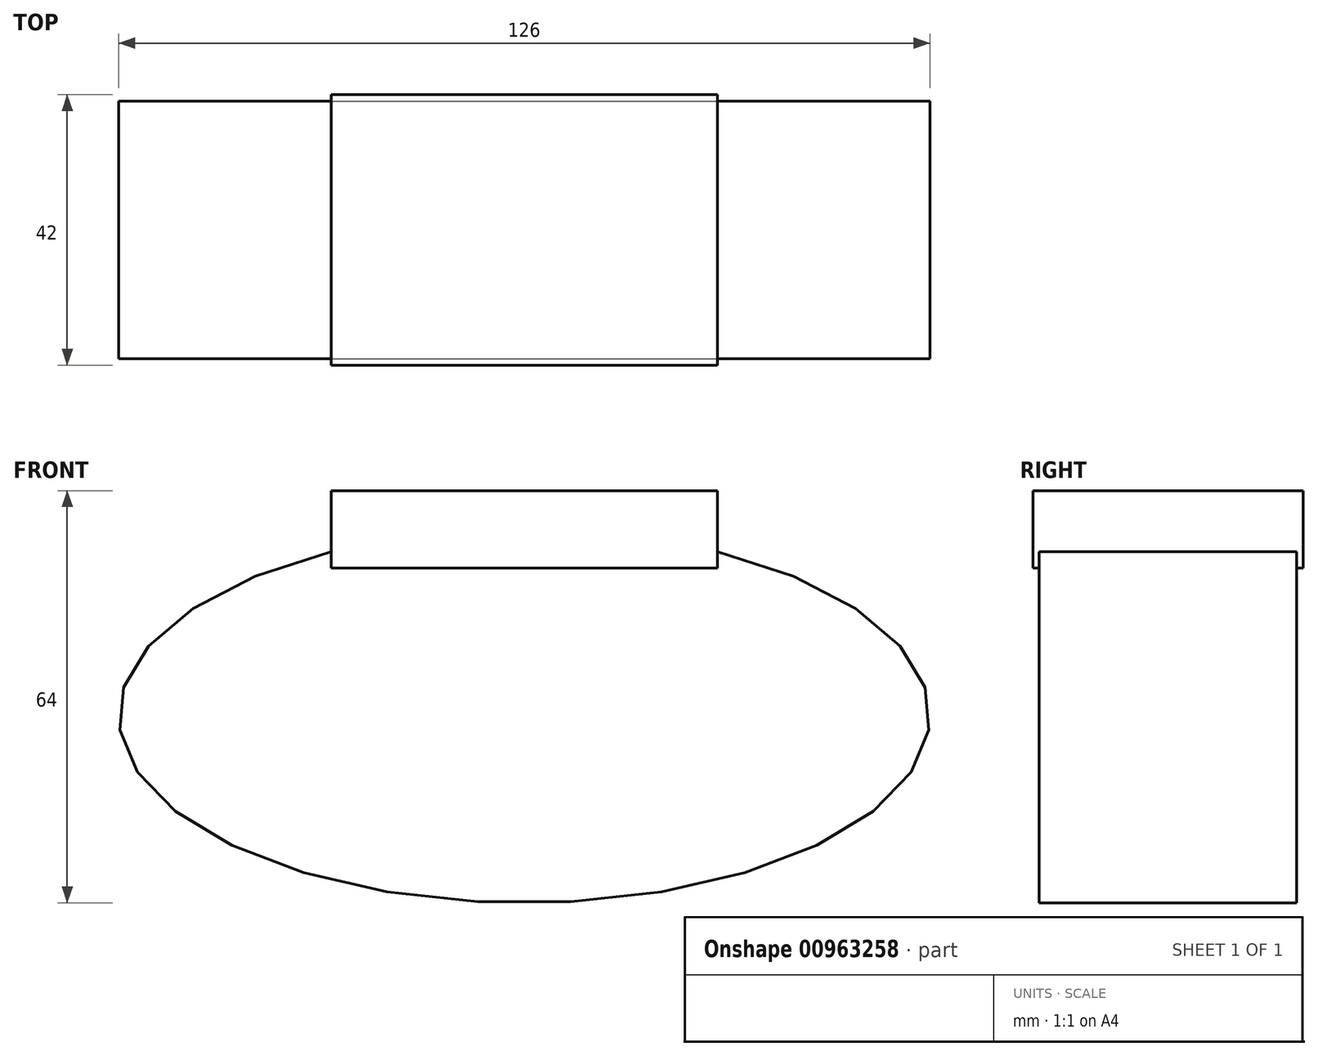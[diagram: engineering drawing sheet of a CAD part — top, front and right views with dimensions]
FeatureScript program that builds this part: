
annotation { "Feature Type Name" : "Feature", "Feature Type Description" : "" }
export const myFeature = defineFeature(function(context is Context, id is Id, definition is map)
    precondition{}
    {
        {
            var Q0;
            Q0=qCreatedBy(makeId("Front.planeOp"),FACE);
            var sketch = newSketch(context, id + "F0", { "sketchPlane" : qUnion([Q0])});
            skEllipse(sketch, "E0", {"center": v(0, 0) * mm, "majorRadius": 63 * mm, "minorRadius": 29 * mm, "majorAxis": v(1, 0)});
            skSolve(sketch);
        }
        {
            var Q0;
            Q0=makeQuery(id+"F0.imprint","IMPRINT",FACE,{"disambiguationData":[TD([[makeQuery(id+"F0.imprint","IMPRINT",EDGE,{"derivedFrom":sQuery(id+"F0.wireOp",EDGE,"E0")}),1.0]])]});
            extrude(context, id + "F1", {"entities" : qUnion([Q0]), "depth" : 40 * mm, "offsetDistance" : 25 * mm});
        }
        {
            var Q0;
            Q0=qCreatedBy(makeId("Front.planeOp"),FACE);
            cPlane(context, id + "F2", {"entities" : qUnion([Q0]), "cplaneType" : CPlaneType.OFFSET, "offset" : 20 * mm, "width" : 150 * mm, "height" : 150 * mm});
        }
        {
            var Q0;
            Q0=qCreatedBy(id+"F2.planeOp",FACE);
            var sketch = newSketch(context, id + "F3", { "sketchPlane" : qUnion([Q0])});
            skLineSegment(sketch, "E1.bottom", {"start": v(30, 23) * mm, "end": v(-30, 23) * mm});
            skLineSegment(sketch, "E1.top", {"start": v(30, 35) * mm, "end": v(-30, 35) * mm});
            skLineSegment(sketch, "E1.left", {"start": v(30, 23) * mm, "end": v(30, 35) * mm});
            skLineSegment(sketch, "E1.right", {"start": v(-30, 23) * mm, "end": v(-30, 35) * mm});
            skPoint(sketch, "E1.middle", {"position": v(0, 29) * mm});
            skSolve(sketch);
        }
        {
            var Q0;
            Q0=makeQuery(id+"F3.imprint","IMPRINT",FACE,{"disambiguationData":[TD([[makeQuery(id+"F3.imprint","IMPRINT",EDGE,{"derivedFrom":sQuery(id+"F3.wireOp",EDGE,"E1.bottom")}),-1.0]])]});
            extrude(context, id + "F4", {"entities" : qUnion([Q0]), "operationType" : NewBodyOperationType.ADD, "surfaceOperationType" : NewSurfaceOperationType.ADD, "endBound" : BoundingType.SYMMETRIC, "depth" : 42 * mm, "offsetDistance" : 25 * mm});
        }
    });
